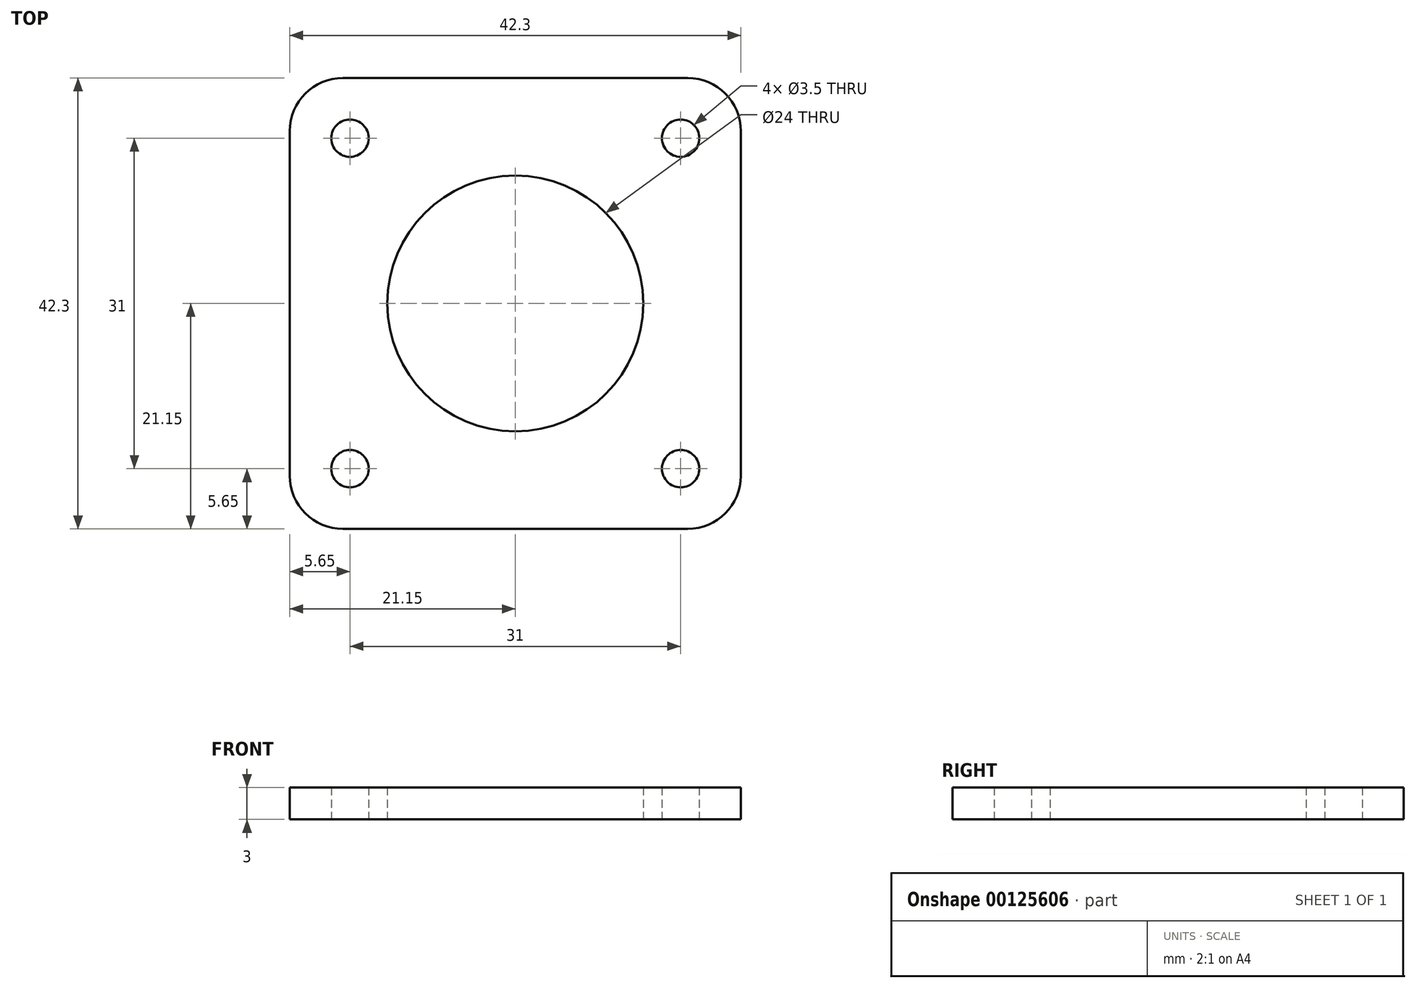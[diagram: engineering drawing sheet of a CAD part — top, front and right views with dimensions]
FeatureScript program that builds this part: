
annotation { "Feature Type Name" : "Feature", "Feature Type Description" : "" }
export const myFeature = defineFeature(function(context is Context, id is Id, definition is map)
    precondition{}
    {
        {
            var Q0;
            Q0=qCreatedBy(makeId("Top.planeOp"),FACE);
            var sketch = newSketch(context, id + "F0", { "sketchPlane" : qUnion([Q0])});
            skCircle(sketch, "E0.0", {"center": v(0, 0) * mm, "radius": 1.75 * mm});
            skCircle(sketch, "E0.1", {"center": v(31, 0) * mm, "radius": 1.75 * mm});
            skCircle(sketch, "E0.2", {"center": v(31, -31) * mm, "radius": 1.75 * mm});
            skCircle(sketch, "E0.3", {"center": v(0, -31) * mm, "radius": 1.75 * mm});
            skLineSegment(sketch, "E1.bottom", {"start": v(-0.65, 5.65) * mm, "end": v(31.65, 5.65) * mm});
            skLineSegment(sketch, "E1.top", {"start": v(-0.65, -36.65) * mm, "end": v(31.65, -36.65) * mm});
            skLineSegment(sketch, "E1.left", {"start": v(-5.65, 0.65) * mm, "end": v(-5.65, -31.65) * mm});
            skLineSegment(sketch, "E1.right", {"start": v(36.65, 0.65) * mm, "end": v(36.65, -31.65) * mm});
            skLineSegment(sketch, "E2", {"start": v(-5.65, 5.65) * mm, "end": v(36.65, -36.65) * mm, "construction": true});
            skPoint(sketch, "E3.visualSharp", {"position": v(-5.65, 5.65) * mm});
            skArc(sketch, "E3.filletArc", {"start": v(-0.65, 5.65) * mm, "mid": v(-4.19, 4.19) * mm, "end": v(-5.65, 0.65) * mm});
            skPoint(sketch, "E4.visualSharp", {"position": v(36.65, 5.65) * mm});
            skArc(sketch, "E4.filletArc", {"start": v(36.65, 0.65) * mm, "mid": v(35.19, 4.19) * mm, "end": v(31.65, 5.65) * mm});
            skPoint(sketch, "E5.visualSharp", {"position": v(36.65, -36.65) * mm});
            skArc(sketch, "E5.filletArc", {"start": v(31.65, -36.65) * mm, "mid": v(35.19, -35.19) * mm, "end": v(36.65, -31.65) * mm});
            skPoint(sketch, "E6.visualSharp", {"position": v(-5.65, -36.65) * mm});
            skArc(sketch, "E6.filletArc", {"start": v(-5.65, -31.65) * mm, "mid": v(-4.19, -35.19) * mm, "end": v(-0.65, -36.65) * mm});
            skCircle(sketch, "E7", {"center": v(15.5, -15.5) * mm, "radius": 12 * mm});
            skSolve(sketch);
        }
        {
            var Q0;
            Q0=makeQuery(id+"F0.imprint","IMPRINT",FACE,{"disambiguationData":[TD([[makeQuery(id+"F0.imprint","IMPRINT",EDGE,{"derivedFrom":sQuery(id+"F0.wireOp",EDGE,"E0.0")}),-1.0]])]});
            extrude(context, id + "F1", {"entities" : qUnion([Q0]), "depth" : 3 * mm});
        }
    });
